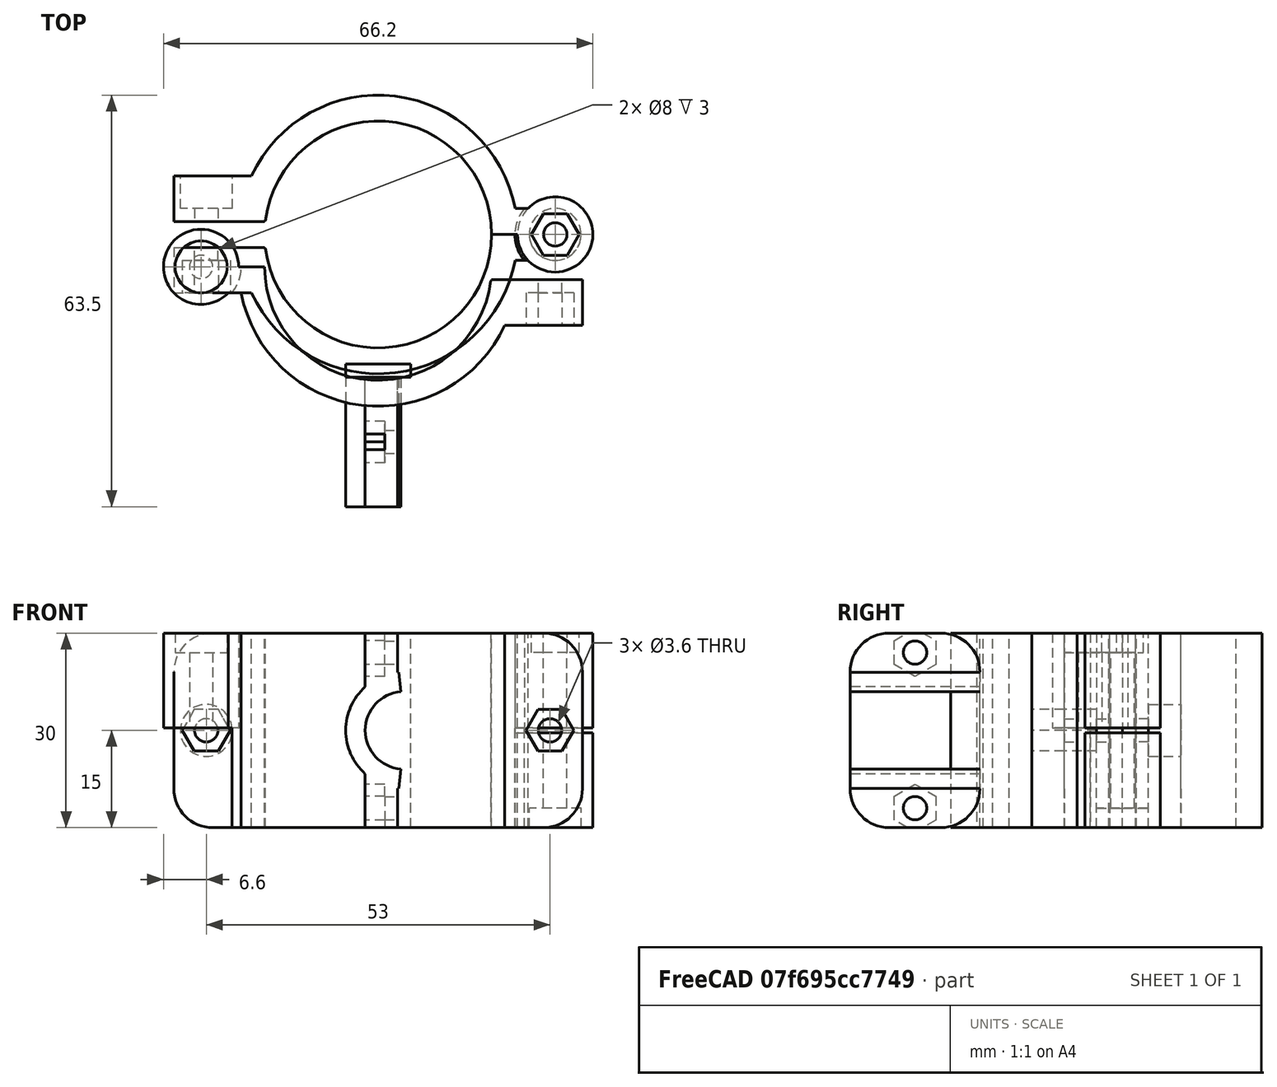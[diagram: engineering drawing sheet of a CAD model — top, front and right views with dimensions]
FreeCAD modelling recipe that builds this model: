
FCSTD DOCUMENT  (FreeCAD 0.18.4R)
Label: pipe_attach_v2
License: All rights reserved
LicenseURL: http://en.wikipedia.org/wiki/All_rights_reserved
objects: Part::Cylinder×8, Part::MultiFuse×4, PartDesign::FeatureBase×4, PartDesign::Body×4, Part::Box×3, Part::Cut×3, Part::Mirroring×2, Part::Compound×2, Part::Feature×2, Spreadsheet::Sheet×1, Part::Fillet×1, Part::RegularPolygon×1, Part::Extrusion×1
note: 35 computed .brp shape members not serialized (recipe doc carries the construction recipe); baked Part::Feature solids carry a one-line shape summary decoded from their .brp

FEATURE [Spreadsheet::Sheet] Spreadsheet  label="p001"
  cells = A1=internal_r; B1(internal_r)=17.5; A2=wall; B2(wall)=4; A3=length; B3(length)=30; A4=hole_r; B4(hole_r)=1.8; A5=petal_size; B5(petal_size)=10; A6=bolt_head_nut_height; B6(bolt_head_nut_height)=3; A7=bolt_head_r; B7(bolt_head_r)=4; A8=m3_nut_circumradius; B8(m3_nut_circumradius)=3.7; A9=petal_offset; B9(petal_offset)=2; A10=external_cylinder_angle_offset; B10(external_cylinder_angle_offset)=7
FEATURE [Part::Cylinder] Cylinder  label="external cylinder"
  Angle = 173
  AttacherType = Attacher::AttachEngine3D
  Height = 30
  Radius = 21.5
  expr: Radius = p001.internal_r + p001.wall
  expr: Angle = 180 - p001.external_cylinder_angle_offset
  expr: Height = p001.length
FEATURE [Part::Cylinder] Cylinder001  label="hole cylinder"
  Angle = 180
  AttacherType = Attacher::AttachEngine3D
  Height = 30
  Radius = 17.5
  expr: Radius = p001.internal_r
  expr: Height = p001.length
FEATURE [Part::Cylinder] Cylinder002  label="side cylinder"
  Angle = 360
  AttacherType = Attacher::AttachEngine3D
  Height = 30
  Placement = pos=(27.3,0,0) rot=(0,0,1;0rad)
  Radius = 5.8
  expr: Placement.Base.x = p001.internal_r + p001.wall + p001.wall + p001.hole_r
  expr: Height = p001.length
  expr: Radius = p001.hole_r + p001.wall
FEATURE [Part::Box] Box  label="petal cube"
  AttacherType = Attacher::AttachEngine3D
  Height = 30
  Length = 14
  Placement = pos=(-31.5,2,0) rot=(0,0,1;0rad)
  Width = 7
  expr: Width = p001.wall + p001.bolt_head_nut_height
  expr: Placement.Base.y = p001.petal_offset
  expr: Placement.Base.x = -(p001.internal_r + p001.wall + p001.petal_size)
  expr: Height = p001.length
  expr: Length = p001.petal_size + p001.wall
FEATURE [Part::Fillet] Fillet  label="petal fillet"
  Base = -> Box
  Edges = 2 edges r=6: [Edge2,Edge4]
FEATURE [Part::Box] Box001  label="side cube"
  AttacherType = Attacher::AttachEngine3D
  Height = 30
  Length = 9.8
  Placement = pos=(17.5,0,0) rot=(0,0,1;0rad)
  Width = 4
  expr: Placement.Base.x = p001.internal_r
  expr: Width = p001.wall
  expr: Height = p001.length
  expr: Length = p001.hole_r + p001.wall * 2
FEATURE [Part::Cylinder] Cylinder003  label="bolt hole"
  Angle = 360
  AttacherType = Attacher::AttachEngine3D
  Height = 50
  Placement = pos=(-26.5,20,15) rot=(1,0,0;1.5708rad)
  Radius = 1.8
  expr: Placement.Base.z = p001.length / 2
  expr: Placement.Base.x = -(p001.internal_r + p001.wall + p001.petal_size / 2)
  expr: Radius = p001.hole_r
FEATURE [Part::Cylinder] Cylinder004  label="horizontal bolt hole"
  Angle = 360
  AttacherType = Attacher::AttachEngine3D
  Height = 30
  Placement = pos=(27.3,0,0) rot=(0,0,1;0rad)
  Radius = 1.8
  expr: Height = p001.length
  expr: Placement.Base.x = p001.internal_r + p001.wall * 2 + p001.hole_r
  expr: Radius = p001.hole_r
FEATURE [Part::MultiFuse] Fusion  label="hole fusion"
  Shapes = -> [Cylinder004,Cylinder003,Cylinder001]
FEATURE [Part::MultiFuse] Fusion001  label="half fusion"
  Shapes = -> [Box001,Fillet,Cylinder002,Cylinder]
FEATURE [Part::Cut] Cut  label="attach half"
  Base = -> Fusion001
  Tool = -> Fusion
FEATURE [Part::Mirroring] Part__Mirroring  label="attach half (Mirror #1)"
  Base = (0,0,0)
  Normal = (0,1,0)
  Source = -> Cut
FEATURE [Part::Cylinder] Cylinder005  label="side half cut cylinder"
  Angle = 360
  AttacherType = Attacher::AttachEngine3D
  Height = 15.4
  Placement = pos=(27.3,0,0) rot=(0,0,1;0rad)
  Radius = 6.2
  expr: Placement.Base.x = p001.internal_r + p001.wall + p001.wall + p001.hole_r
  expr: Height = p001.length / 2 + 0.4
  expr: Radius = p001.wall + p001.hole_r + 0.4
FEATURE [Part::Mirroring] Part__Mirroring001  label="side half cut cylinder (Mirror #2)"
  Base = (0,0,15)
  Normal = (0,0,1)
  Source = -> Cylinder005
  expr: Base.z = p001.length / 2
FEATURE [Part::Cylinder] Cylinder095  label="bolt head cylinder"
  Angle = 360
  AttacherType = Attacher::AttachEngine3D
  Height = 20
  Placement = pos=(-26.5,4,15) rot=(-1,0,0;1.5708rad)
  Radius = 4
  expr: Placement.Base.z = p001.length / 2
  expr: Placement.Base.y = p001.wall
  expr: Placement.Base.x = -(p001.internal_r + p001.wall + p001.petal_size / 2)
  expr: Radius = p001.bolt_head_r
FEATURE [Part::RegularPolygon] RegularPolygon003  label="m3 nut polygon"
  AttacherType = Attacher::AttachEngine3D
  Circumradius = 3.7
  Polygon = 6
  expr: Circumradius = p001.m3_nut_circumradius
FEATURE [Part::Extrusion] Extrude003  label="m3 nut hole"
  Base = -> RegularPolygon003
  Dir = (0,0,1)
  DirMode = 2
  FaceMakerClass = Part::FaceMakerBullseye
  LengthFwd = 20
  LengthRev = 0
  Solid = true
  Symmetric = false
FEATURE [PartDesign::FeatureBase] Clone
  BaseFeature = -> Extrude003
FEATURE [PartDesign::Body] Body  label="m3 nut hole side clone"
  BaseFeature = -> Extrude003
  Group = -> [Clone]
  Origin = -> Origin001
  Placement = pos=(27.3,0,27) rot=(0,0,1;0rad)
  Tip = -> Clone
  expr: Placement.Base.z = p001.length - p001.bolt_head_nut_height
  expr: Placement.Base.x = p001.internal_r + p001.wall * 2 + p001.hole_r
FEATURE [PartDesign::FeatureBase] Clone001
  BaseFeature = -> Extrude003
FEATURE [PartDesign::Body] Body001  label="m3 nut hole petal clone"
  BaseFeature = -> Extrude003
  Group = -> [Clone001]
  Origin = -> Origin002
  Placement = pos=(-26.5,-4,15) rot=(1,0,0;1.5708rad)
  Tip = -> Clone001
  expr: Placement.Base.z = p001.length / 2
  expr: Placement.Base.y = -p001.wall
  expr: Placement.Base.x = -(p001.internal_r + p001.wall + p001.petal_size / 2)
FEATURE [Part::Cylinder] Cylinder096  label="bolt head side cylinder"
  Angle = 360
  AttacherType = Attacher::AttachEngine3D
  Height = 3
  Placement = pos=(27.3,0,0) rot=(0,0,1;0rad)
  Radius = 4
  expr: Height = p001.bolt_head_nut_height
  expr: Placement.Base.x = p001.internal_r + p001.wall * 2 + p001.hole_r
  expr: Radius = p001.bolt_head_r
FEATURE [Part::MultiFuse] Fusion002  label="top half removal"
  Shapes = -> [Body,Cylinder005,Cylinder095]
FEATURE [Part::Cut] Cut001  label="top half cut"
  Base = -> Cut
  Tool = -> Fusion002
FEATURE [Part::MultiFuse] Fusion003  label="botom half fusion"
  Shapes = -> [Part__Mirroring001,Body001,Cylinder096]
FEATURE [Part::Cut] Cut002  label="bottom half cut"
  Base = -> Part__Mirroring
  Tool = -> Fusion003
FEATURE [PartDesign::FeatureBase] Clone002
  BaseFeature = -> Cut001
FEATURE [PartDesign::Body] Body002  label="top half clone"
  BaseFeature = -> Cut001
  Group = -> [Clone002]
  Origin = -> Origin003
  Tip = -> Clone002
FEATURE [PartDesign::FeatureBase] Clone003
  BaseFeature = -> Cut002
FEATURE [PartDesign::Body] Body003  label="bottom half clone"
  BaseFeature = -> Cut002
  Group = -> [Clone003]
  Origin = -> Origin004
  Placement = pos=(0,-5,30) rot=(0,1,0;3.14159rad)
  Tip = -> Clone003
  expr: Placement.Base.z = p001.length
FEATURE [Part::Compound] Compound  label="halves compound"
  Links = -> [Body003,Body002]
FEATURE [Part::Feature] Cut002001  label="bottom half cut 35mm"
  shape: bbox 64.6 x 27.3 x 30 mm, 27 faces (baked)
FEATURE [Part::Box] Box002  label="glue cube"
  AttacherType = Attacher::AttachEngine3D
  Height = 30
  Length = 10
  Placement = pos=(-5,-22,0) rot=(0,0,1;0rad)
  Width = 2
  expr: Height = p001.length
FEATURE [Part::Feature] Cut002002  label="bottom half 12mm001"
  Placement = pos=(4,-22,15) rot=(-0.57735,-0.57735,0.57735;4.18879rad)
  shape: bbox 8.477 x 20 x 30 mm, 34 faces (baked)
FEATURE [Part::Compound] Compound001  label="bottom 35-12 compound"
  Links = -> [Cut002001,Box002,Cut002002]
